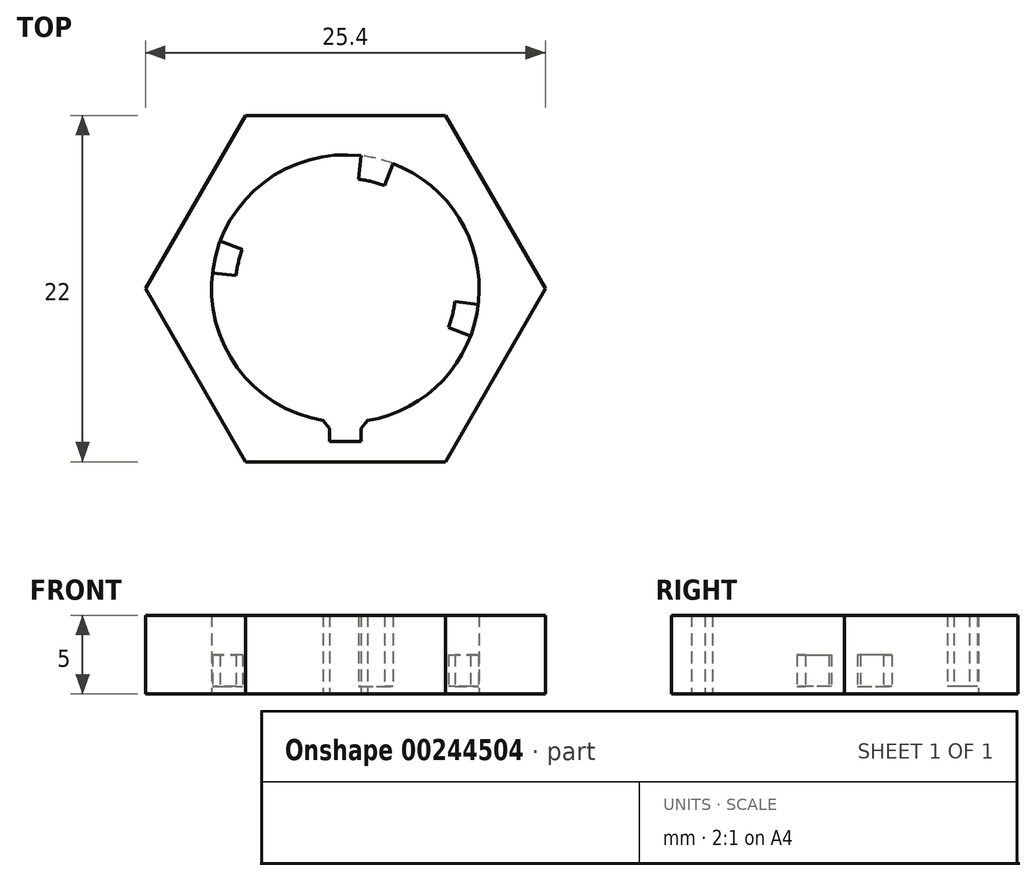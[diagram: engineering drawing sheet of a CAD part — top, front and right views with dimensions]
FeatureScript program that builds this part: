
annotation { "Feature Type Name" : "Feature", "Feature Type Description" : "" }
export const myFeature = defineFeature(function(context is Context, id is Id, definition is map)
    precondition{}
    {
        {
            var Q0;
            Q0=qCreatedBy(makeId("Top.planeOp"),FACE);
            var sketch = newSketch(context, id + "F0", { "sketchPlane" : qUnion([Q0])});
            skLineSegment(sketch, "E0.0", {"start": v(-12.7, 0) * mm, "end": v(-6.35, 11) * mm});
            skLineSegment(sketch, "E0.1", {"start": v(-6.35, 11) * mm, "end": v(6.35, 11) * mm});
            skLineSegment(sketch, "E0.2", {"start": v(6.35, 11) * mm, "end": v(12.7, 0) * mm});
            skLineSegment(sketch, "E0.3", {"start": v(12.7, 0) * mm, "end": v(6.35, -11) * mm});
            skLineSegment(sketch, "E0.4", {"start": v(6.35, -11) * mm, "end": v(-6.35, -11) * mm});
            skLineSegment(sketch, "E0.5", {"start": v(-6.35, -11) * mm, "end": v(-12.7, 0) * mm});
            skArc(sketch, "E1", {"start": v(1, 8.44) * mm, "mid": v(-4.4, 7.27) * mm, "end": v(-7.95, 3.01) * mm});
            skLineSegment(sketch, "E2.left", {"start": v(1, -8.44) * mm, "end": v(1, -9.72) * mm});
            skLineSegment(sketch, "E2.right", {"start": v(-1, -8.44) * mm, "end": v(-1, -9.72) * mm});
            skPoint(sketch, "E2.middle", {"position": v(0, -11) * mm});
            skPoint(sketch, "E2.top.end.orphan", {"position": v(-1, -15) * mm});
            skPoint(sketch, "E3.orphan", {"position": v(1, -15) * mm});
            skPoint(sketch, "E2.bottom.end.orphan", {"position": v(-1, -7) * mm});
            skPoint(sketch, "E4.orphan", {"position": v(1, -7) * mm});
            skLineSegment(sketch, "E5", {"start": v(1, -9.72) * mm, "end": v(-1, -9.72) * mm});
            skPoint(sketch, "E6.orphan", {"position": v(1, -11) * mm});
            skPoint(sketch, "E7.orphan", {"position": v(-1, -11) * mm});
            skLineSegment(sketch, "E8", {"start": v(0.82, 6.95) * mm, "end": v(1, 8.44) * mm});
            skLineSegment(sketch, "E9", {"start": v(1, 8.44) * mm, "end": v(0.82, 6.95) * mm});
            skLineSegment(sketch, "E10", {"start": v(2.48, 6.55) * mm, "end": v(3.01, 7.95) * mm});
            skArc(sketch, "E11", {"start": v(2.48, 6.55) * mm, "mid": v(1.66, 6.8) * mm, "end": v(0.82, 6.95) * mm});
            skLineSegment(sketch, "E12.1.0", {"start": v(-6.55, 2.48) * mm, "end": v(-7.95, 3.01) * mm});
            skLineSegment(sketch, "E12.1.1", {"start": v(-8.44, 1) * mm, "end": v(-6.95, 0.82) * mm});
            skArc(sketch, "E12.1.2", {"start": v(-6.55, 2.48) * mm, "mid": v(-6.8, 1.66) * mm, "end": v(-6.95, 0.82) * mm});
            skLineSegment(sketch, "E12.3.0", {"start": v(6.55, -2.48) * mm, "end": v(7.95, -3.01) * mm});
            skLineSegment(sketch, "E12.3.1", {"start": v(8.44, -1) * mm, "end": v(6.95, -0.82) * mm});
            skArc(sketch, "E12.3.2", {"start": v(6.55, -2.48) * mm, "mid": v(6.8, -1.66) * mm, "end": v(6.95, -0.82) * mm});
            skArc(sketch, "E13.trimOffspring", {"start": v(-8.44, 1) * mm, "mid": v(-2.02, -8.26) * mm, "end": v(7.95, -3.01) * mm});
            skArc(sketch, "E14.trimOffspring", {"start": v(8.44, -1) * mm, "mid": v(7.27, 4.4) * mm, "end": v(3.01, 7.95) * mm});
            skSolve(sketch);
        }
        {
            var Q0;
            Q0 = qSketchRegion(id + "F0", true);
            extrude(context, id + "F1", {"entities" : qUnion([Q0]), "depth" : 5 * mm});
        }
        {
            var Q0;
            Q0=makeQuery(id+"F1.opExtrude","CAP_FACE",FACE,{"disambiguationData":[OSD([sQuery(id+"F0.wireOp",EDGE,"E0.0"),sQuery(id+"F0.wireOp",EDGE,"E0.1"),sQuery(id+"F0.wireOp",EDGE,"E0.2"),sQuery(id+"F0.wireOp",EDGE,"E0.3"),sQuery(id+"F0.wireOp",EDGE,"E0.4"),sQuery(id+"F0.wireOp",EDGE,"E0.5"),sQuery(id+"F0.wireOp",EDGE,"E1"),sQuery(id+"F0.wireOp",EDGE,"E2.right"),sQuery(id+"F0.wireOp",EDGE,"E2.left"),sQuery(id+"F0.wireOp",EDGE,"E5"),sQuery(id+"F0.wireOp",EDGE,"E9"),sQuery(id+"F0.wireOp",EDGE,"E10"),sQuery(id+"F0.wireOp",EDGE,"E11"),sQuery(id+"F0.wireOp",EDGE,"E12.1.0"),sQuery(id+"F0.wireOp",EDGE,"E12.1.1"),sQuery(id+"F0.wireOp",EDGE,"E12.1.2"),sQuery(id+"F0.wireOp",EDGE,"E12.3.0"),sQuery(id+"F0.wireOp",EDGE,"E12.3.1"),sQuery(id+"F0.wireOp",EDGE,"E12.3.2"),sQuery(id+"F0.wireOp",EDGE,"E13.trimOffspring"),sQuery(id+"F0.wireOp",EDGE,"E14.trimOffspring")])],"isStart":false});
            var sketch = newSketch(context, id + "F2", { "sketchPlane" : qUnion([Q0])});
            skCircle(sketch, "E15", {"center": v(0, 0) * mm, "radius": 8.5 * mm});
            skSolve(sketch);
        }
        {
            var Q0;
            {var subQ1=makeQuery(id+"F1.opExtrude","CAP_EDGE",EDGE,{"disambiguationData":[OSD([sQuery(id+"F0.wireOp",EDGE,"E12.1.0")])],"isStart":false});Q0=makeQuery(id+"F2.imprint","IMPRINT",FACE,{"disambiguationData":[TD([[makeQuery(id+"F2.imprint","IMPRINT",EDGE,{"derivedFrom":subQ1}),1.0]])]});}
            var Q1;
            {var subQ1=makeQuery(id+"F1.opExtrude","CAP_EDGE",EDGE,{"disambiguationData":[OSD([sQuery(id+"F0.wireOp",EDGE,"E9")])],"isStart":false});Q1=makeQuery(id+"F2.imprint","IMPRINT",FACE,{"disambiguationData":[TD([[makeQuery(id+"F2.imprint","IMPRINT",EDGE,{"derivedFrom":subQ1}),1.0]])]});}
            var Q2;
            {var subQ1=makeQuery(id+"F1.opExtrude","CAP_EDGE",EDGE,{"disambiguationData":[OSD([sQuery(id+"F0.wireOp",EDGE,"E12.3.0")])],"isStart":false});Q2=makeQuery(id+"F2.imprint","IMPRINT",FACE,{"disambiguationData":[TD([[makeQuery(id+"F2.imprint","IMPRINT",EDGE,{"derivedFrom":subQ1}),1.0]])]});}
            extrude(context, id + "F3", {"entities" : qUnion([Q0, Q1, Q2]), "operationType" : NewBodyOperationType.REMOVE, "oppositeDirection" : true, "depth" : 2.5 * mm});
        }
        {
            var Q0;
            Q0=makeQuery(id+"F1.opExtrude","CAP_FACE",FACE,{"disambiguationData":[OSD([sQuery(id+"F0.wireOp",EDGE,"E0.0"),sQuery(id+"F0.wireOp",EDGE,"E0.1"),sQuery(id+"F0.wireOp",EDGE,"E0.2"),sQuery(id+"F0.wireOp",EDGE,"E0.3"),sQuery(id+"F0.wireOp",EDGE,"E0.4"),sQuery(id+"F0.wireOp",EDGE,"E0.5"),sQuery(id+"F0.wireOp",EDGE,"E1"),sQuery(id+"F0.wireOp",EDGE,"E2.right"),sQuery(id+"F0.wireOp",EDGE,"E2.left"),sQuery(id+"F0.wireOp",EDGE,"E5"),sQuery(id+"F0.wireOp",EDGE,"E9"),sQuery(id+"F0.wireOp",EDGE,"E10"),sQuery(id+"F0.wireOp",EDGE,"E11"),sQuery(id+"F0.wireOp",EDGE,"E12.1.0"),sQuery(id+"F0.wireOp",EDGE,"E12.1.1"),sQuery(id+"F0.wireOp",EDGE,"E12.1.2"),sQuery(id+"F0.wireOp",EDGE,"E12.3.0"),sQuery(id+"F0.wireOp",EDGE,"E12.3.1"),sQuery(id+"F0.wireOp",EDGE,"E12.3.2"),sQuery(id+"F0.wireOp",EDGE,"E13.trimOffspring"),sQuery(id+"F0.wireOp",EDGE,"E14.trimOffspring")])],"isStart":true});
            var sketch = newSketch(context, id + "F4", { "sketchPlane" : qUnion([Q0])});
            skCircle(sketch, "E16", {"center": v(0, 0) * mm, "radius": 8.5 * mm});
            skSolve(sketch);
        }
        {
            var Q0;
            Q0 = qSketchRegion(id + "F4", true);
            extrude(context, id + "F5", {"entities" : qUnion([Q0]), "operationType" : NewBodyOperationType.REMOVE, "oppositeDirection" : true, "depth" : .5 * mm});
        }
        {
            var Q0;
            Q0=makeQuery(id+"F1.opExtrude","SWEPT_EDGE",EDGE,{"disambiguationData":[OSD([sQuery(id+"F0.wireOp",EDGE,"E2.right"),sQuery(id+"F0.wireOp",EDGE,"E13.trimOffspring")])]});
            var Q1;
            Q1=makeQuery(id+"F1.opExtrude","SWEPT_EDGE",EDGE,{"disambiguationData":[OSD([sQuery(id+"F0.wireOp",EDGE,"E2.left"),sQuery(id+"F0.wireOp",EDGE,"E13.trimOffspring")])]});
            chamfer(context, id + "F6", {"entities" : qUnion([Q0, Q1]), "width" : .5 * mm, "tangentPropagation" : true});
        }
    });
